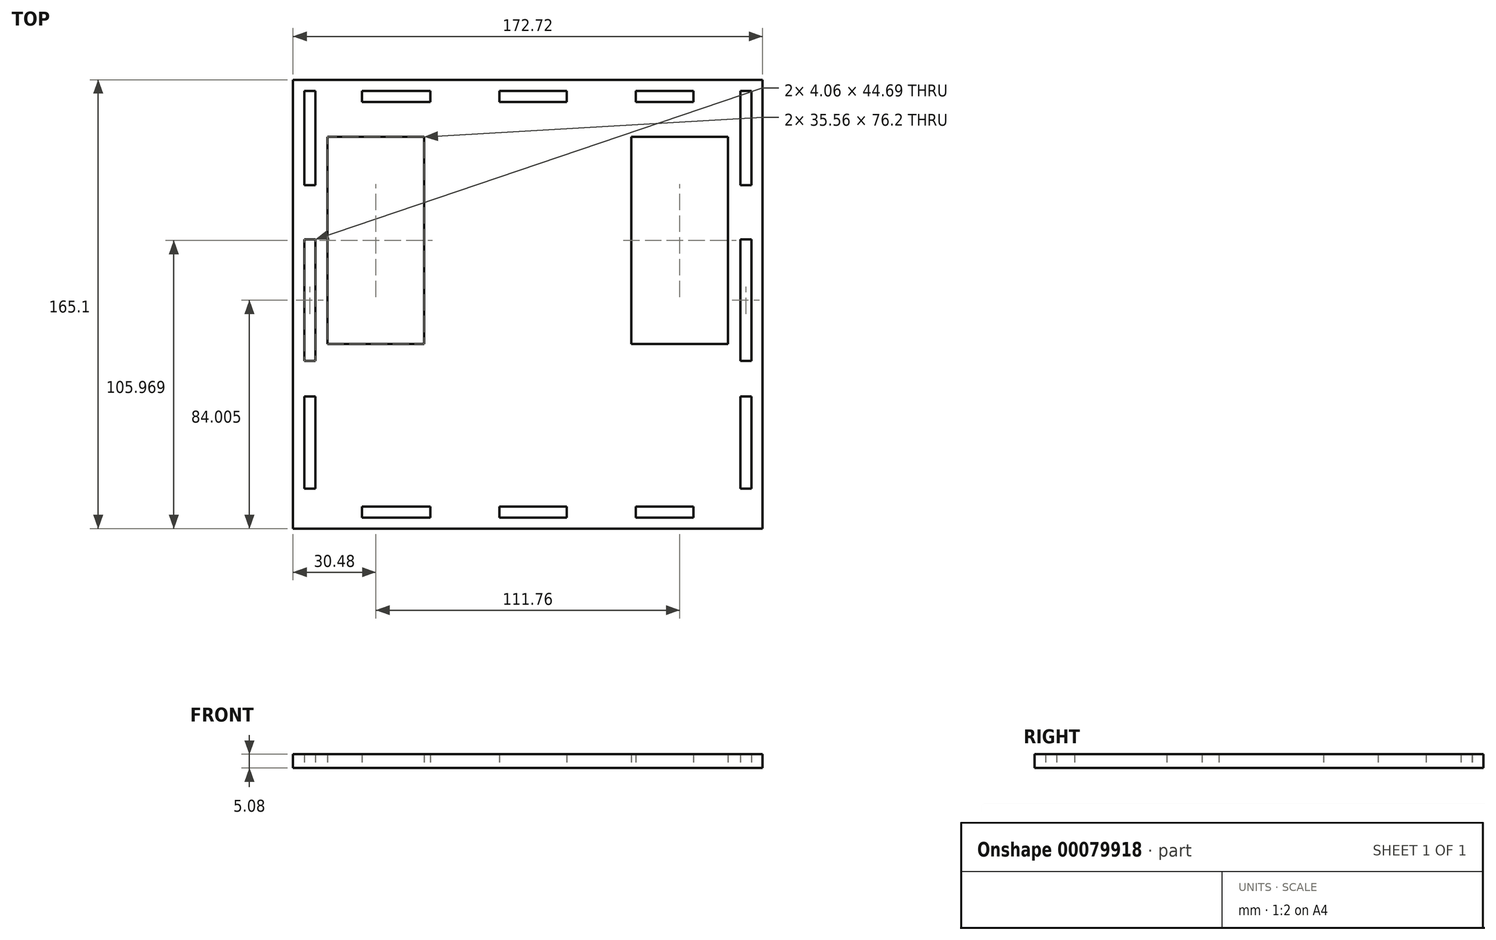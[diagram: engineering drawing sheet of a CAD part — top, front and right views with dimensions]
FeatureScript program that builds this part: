
annotation { "Feature Type Name" : "Feature", "Feature Type Description" : "" }
export const myFeature = defineFeature(function(context is Context, id is Id, definition is map)
    precondition{}
    {
        {
            var Q0;
            Q0=qCreatedBy(makeId("Top.planeOp"),FACE);
            var sketch = newSketch(context, id + "F0", { "sketchPlane" : qUnion([Q0])});
            skLineSegment(sketch, "E0.bottom", {"start": v(-86.36, 49.34) * mm, "end": v(86.36, 49.34) * mm});
            skLineSegment(sketch, "E0.top", {"start": v(-86.36, -115.76) * mm, "end": v(86.36, -115.76) * mm});
            skLineSegment(sketch, "E0.left", {"start": v(-86.36, 49.34) * mm, "end": v(-86.36, -115.76) * mm});
            skLineSegment(sketch, "E0.right", {"start": v(86.36, 49.34) * mm, "end": v(86.36, -115.76) * mm});
            skLineSegment(sketch, "E1.bottom", {"start": v(-73.66, 28.3) * mm, "end": v(-38.1, 28.3) * mm});
            skLineSegment(sketch, "E1.top", {"start": v(-73.66, -47.9) * mm, "end": v(-38.1, -47.9) * mm});
            skLineSegment(sketch, "E1.left", {"start": v(-73.66, 28.3) * mm, "end": v(-73.66, -47.9) * mm});
            skLineSegment(sketch, "E1.right", {"start": v(-38.1, 28.3) * mm, "end": v(-38.1, -47.9) * mm});
            skLineSegment(sketch, "E2.bottom", {"start": v(-82.25, 45.3) * mm, "end": v(-78.18, 45.3) * mm});
            skLineSegment(sketch, "E2.top", {"start": v(-82.25, 10.6) * mm, "end": v(-78.18, 10.6) * mm});
            skLineSegment(sketch, "E2.left", {"start": v(-78.18, 45.3) * mm, "end": v(-78.18, 10.6) * mm});
            skLineSegment(sketch, "E2.right", {"start": v(-82.25, 45.3) * mm, "end": v(-82.25, 10.6) * mm});
            skLineSegment(sketch, "E3.bottom", {"start": v(-82.25, -9.4) * mm, "end": v(-78.18, -9.4) * mm});
            skLineSegment(sketch, "E3.top", {"start": v(-82.25, -54.1) * mm, "end": v(-78.18, -54.1) * mm});
            skLineSegment(sketch, "E3.left", {"start": v(-78.18, -9.4) * mm, "end": v(-78.18, -54.1) * mm});
            skLineSegment(sketch, "E3.right", {"start": v(-82.25, -9.4) * mm, "end": v(-82.25, -54.1) * mm});
            skLineSegment(sketch, "E4.bottom", {"start": v(-82.25, -67.1) * mm, "end": v(-78.18, -67.1) * mm});
            skLineSegment(sketch, "E4.top", {"start": v(-82.25, -101.03) * mm, "end": v(-78.18, -101.03) * mm});
            skLineSegment(sketch, "E4.left", {"start": v(-78.18, -67.1) * mm, "end": v(-78.18, -101.03) * mm});
            skLineSegment(sketch, "E4.right", {"start": v(-82.25, -67.1) * mm, "end": v(-82.25, -101.03) * mm});
            skLineSegment(sketch, "E5", {"start": v(0, 49.34) * mm, "end": v(0, -115.76) * mm, "construction": true});
            skLineSegment(sketch, "E6.MirrorCS", {"start": v(82.25, 45.3) * mm, "end": v(82.25, 10.6) * mm});
            skLineSegment(sketch, "E7.MirrorCS", {"start": v(78.18, 45.3) * mm, "end": v(78.18, 10.6) * mm});
            skLineSegment(sketch, "E8.MirrorCS", {"start": v(82.25, -9.4) * mm, "end": v(82.25, -54.1) * mm});
            skLineSegment(sketch, "E9.MirrorCS", {"start": v(78.18, -9.4) * mm, "end": v(78.18, -54.1) * mm});
            skLineSegment(sketch, "E10.MirrorCS", {"start": v(82.25, -67.1) * mm, "end": v(82.25, -101.03) * mm});
            skLineSegment(sketch, "E11.MirrorCS", {"start": v(78.18, -67.1) * mm, "end": v(78.18, -101.03) * mm});
            skLineSegment(sketch, "E12.MirrorCS", {"start": v(82.25, -67.1) * mm, "end": v(78.18, -67.1) * mm});
            skLineSegment(sketch, "E13.MirrorCS", {"start": v(82.25, -101.03) * mm, "end": v(78.18, -101.03) * mm});
            skLineSegment(sketch, "E14.MirrorCS", {"start": v(82.25, -54.1) * mm, "end": v(78.18, -54.1) * mm});
            skLineSegment(sketch, "E15.MirrorCS", {"start": v(82.25, -9.4) * mm, "end": v(78.18, -9.4) * mm});
            skLineSegment(sketch, "E16.MirrorCS", {"start": v(82.25, 45.3) * mm, "end": v(78.18, 45.3) * mm});
            skLineSegment(sketch, "E17.MirrorCS", {"start": v(82.25, 10.6) * mm, "end": v(78.18, 10.6) * mm});
            skLineSegment(sketch, "E18.MirrorCS", {"start": v(73.66, 28.3) * mm, "end": v(38.1, 28.3) * mm});
            skLineSegment(sketch, "E19.MirrorCS", {"start": v(73.66, 28.3) * mm, "end": v(73.66, -47.9) * mm});
            skLineSegment(sketch, "E20.MirrorCS", {"start": v(38.1, 28.3) * mm, "end": v(38.1, -47.9) * mm});
            skLineSegment(sketch, "E21.MirrorCS", {"start": v(73.66, -47.9) * mm, "end": v(38.1, -47.9) * mm});
            skLineSegment(sketch, "E22.bottom", {"start": v(-60.96, 45.24) * mm, "end": v(-35.86, 45.24) * mm});
            skLineSegment(sketch, "E22.top", {"start": v(-60.96, 41.18) * mm, "end": v(-35.86, 41.18) * mm});
            skLineSegment(sketch, "E22.left", {"start": v(-60.96, 45.24) * mm, "end": v(-60.96, 41.18) * mm});
            skLineSegment(sketch, "E22.right", {"start": v(-35.86, 45.24) * mm, "end": v(-35.86, 41.18) * mm});
            skLineSegment(sketch, "E23.bottom", {"start": v(-10.46, 41.18) * mm, "end": v(14.34, 41.18) * mm});
            skLineSegment(sketch, "E23.top", {"start": v(-10.46, 45.24) * mm, "end": v(14.34, 45.24) * mm});
            skLineSegment(sketch, "E23.left", {"start": v(-10.46, 41.18) * mm, "end": v(-10.46, 45.24) * mm});
            skLineSegment(sketch, "E23.right", {"start": v(14.34, 41.18) * mm, "end": v(14.34, 45.24) * mm});
            skLineSegment(sketch, "E24.bottom", {"start": v(39.74, 45.24) * mm, "end": v(60.96, 45.24) * mm});
            skLineSegment(sketch, "E24.top", {"start": v(39.74, 41.18) * mm, "end": v(60.96, 41.18) * mm});
            skLineSegment(sketch, "E24.left", {"start": v(39.74, 45.24) * mm, "end": v(39.74, 41.18) * mm});
            skLineSegment(sketch, "E24.right", {"start": v(60.96, 45.24) * mm, "end": v(60.96, 41.18) * mm});
            skLineSegment(sketch, "E25", {"start": v(86.36, -33.21) * mm, "end": v(-86.36, -33.21) * mm, "construction": true});
            skLineSegment(sketch, "E26.MirrorCS", {"start": v(39.74, -107.6) * mm, "end": v(60.96, -107.6) * mm});
            skLineSegment(sketch, "E27.MirrorCS", {"start": v(39.74, -111.66) * mm, "end": v(60.96, -111.66) * mm});
            skLineSegment(sketch, "E28.MirrorCS", {"start": v(-10.46, -111.66) * mm, "end": v(14.34, -111.66) * mm});
            skLineSegment(sketch, "E29.MirrorCS", {"start": v(-10.46, -107.6) * mm, "end": v(14.34, -107.6) * mm});
            skLineSegment(sketch, "E30.MirrorCS", {"start": v(-60.96, -107.6) * mm, "end": v(-35.86, -107.6) * mm});
            skLineSegment(sketch, "E31.MirrorCS", {"start": v(-60.96, -111.66) * mm, "end": v(-35.86, -111.66) * mm});
            skLineSegment(sketch, "E32.MirrorCS", {"start": v(60.96, -111.66) * mm, "end": v(60.96, -107.6) * mm});
            skLineSegment(sketch, "E33.MirrorCS", {"start": v(39.74, -111.66) * mm, "end": v(39.74, -107.6) * mm});
            skLineSegment(sketch, "E34.MirrorCS", {"start": v(14.34, -107.6) * mm, "end": v(14.34, -111.66) * mm});
            skLineSegment(sketch, "E35.MirrorCS", {"start": v(-10.46, -107.6) * mm, "end": v(-10.46, -111.66) * mm});
            skLineSegment(sketch, "E36.MirrorCS", {"start": v(-35.86, -111.66) * mm, "end": v(-35.86, -107.6) * mm});
            skLineSegment(sketch, "E37.MirrorCS", {"start": v(-60.96, -111.66) * mm, "end": v(-60.96, -107.6) * mm});
            skSolve(sketch);
        }
        {
            var Q0;
            Q0=makeQuery(id+"F0.imprint","IMPRINT",FACE,{"disambiguationData":[TD([[makeQuery(id+"F0.imprint","IMPRINT",EDGE,{"derivedFrom":sQuery(id+"F0.wireOp",EDGE,"E0.bottom")}),-1.0]])]});
            extrude(context, id + "F1", {"entities" : qUnion([Q0]), "depth" : 5.08 * mm});
        }
    });
